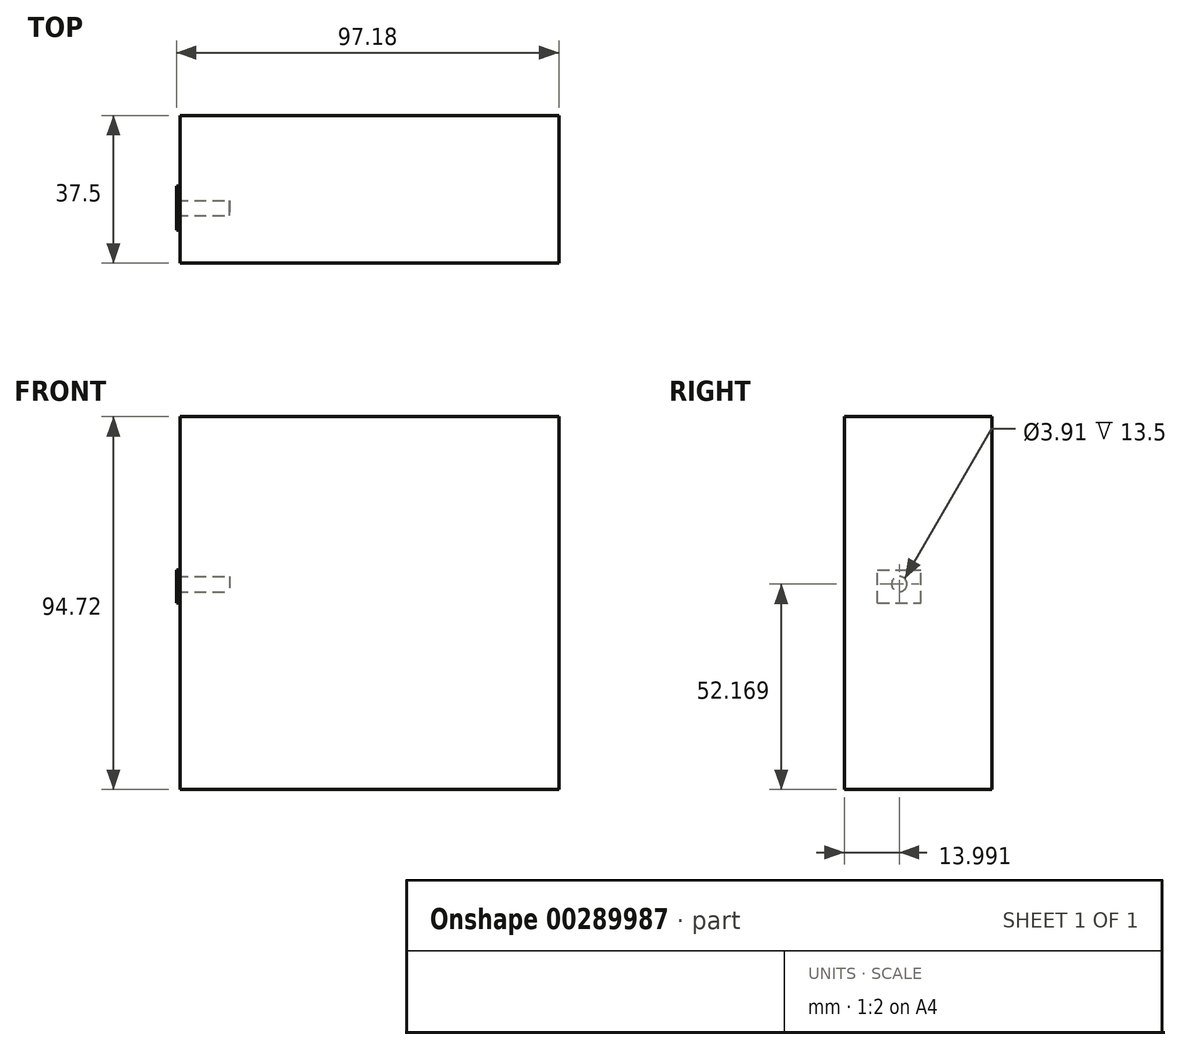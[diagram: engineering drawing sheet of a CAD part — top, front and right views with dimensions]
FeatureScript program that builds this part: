
annotation { "Feature Type Name" : "Feature", "Feature Type Description" : "" }
export const myFeature = defineFeature(function(context is Context, id is Id, definition is map)
    precondition{}
    {
        {
            var Q0;
            Q0=qCreatedBy(makeId("Front.planeOp"),FACE);
            var sketch = newSketch(context, id + "F0", { "sketchPlane" : qUnion([Q0])});
            skLineSegment(sketch, "E0.bottom", {"start": v(48.1, -47.36) * mm, "end": v(-48.1, -47.36) * mm});
            skLineSegment(sketch, "E0.top", {"start": v(48.1, 47.36) * mm, "end": v(-48.1, 47.36) * mm});
            skLineSegment(sketch, "E0.left", {"start": v(48.1, -47.36) * mm, "end": v(48.1, 47.36) * mm});
            skLineSegment(sketch, "E0.right", {"start": v(-48.1, -47.36) * mm, "end": v(-48.1, 47.36) * mm});
            skPoint(sketch, "E0.middle", {"position": v(0, 0) * mm});
            skSolve(sketch);
        }
        {
            var Q0;
            Q0=makeQuery(id+"F0.imprint","IMPRINT",FACE,{"disambiguationData":[TD([[makeQuery(id+"F0.imprint","IMPRINT",EDGE,{"derivedFrom":sQuery(id+"F0.wireOp",EDGE,"E0.bottom")}),-1.0]])]});
            extrude(context, id + "F1", {"entities" : qUnion([Q0]), "oppositeDirection" : true, "depth" : 25 * mm});
        }
        {
            var Q0;
            Q0=makeQuery(id+"F1.opExtrude","SWEPT_FACE",FACE,{"disambiguationData":[OSD([sQuery(id+"F0.wireOp",EDGE,"E0.right")])]});
            var sketch = newSketch(context, id + "F2", { "sketchPlane" : qUnion([Q0])});
            skLineSegment(sketch, "E1.bottom", {"start": v(-8.45, 0) * mm, "end": v(-19.53, 0) * mm});
            skLineSegment(sketch, "E1.top", {"start": v(-8.45, 8.45) * mm, "end": v(-19.53, 8.45) * mm});
            skLineSegment(sketch, "E1.left", {"start": v(-8.45, 0) * mm, "end": v(-8.45, 8.45) * mm});
            skLineSegment(sketch, "E1.right", {"start": v(-19.53, 0) * mm, "end": v(-19.53, 8.45) * mm});
            skPoint(sketch, "E1.middle", {"position": v(-14, 4.23) * mm});
            skPoint(sketch, "E1.cornerSnap0", {"position": v(-25, 0) * mm});
            skSolve(sketch);
        }
        {
            var Q0;
            Q0=makeQuery(id+"F2.imprint","IMPRINT",FACE,{"disambiguationData":[TD([[makeQuery(id+"F2.imprint","IMPRINT",EDGE,{"derivedFrom":sQuery(id+"F2.wireOp",EDGE,"E1.bottom")}),-1.0]])]});
            extrude(context, id + "F3", {"entities" : qUnion([Q0]), "operationType" : NewBodyOperationType.ADD, "depth" : 1 * mm});
        }
        {
            var Q0;
            Q0=makeQuery(id+"F1.opExtrude","CAP_FACE",FACE,{"disambiguationData":[OSD([sQuery(id+"F0.wireOp",EDGE,"E0.bottom"),sQuery(id+"F0.wireOp",EDGE,"E0.top"),sQuery(id+"F0.wireOp",EDGE,"E0.left"),sQuery(id+"F0.wireOp",EDGE,"E0.right")])],"isStart":false});
            var sketch = newSketch(context, id + "F4", { "sketchPlane" : qUnion([Q0])});
            skLineSegment(sketch, "E2.bottom", {"start": v(-48.1, -47.36) * mm, "end": v(48.1, -47.36) * mm});
            skLineSegment(sketch, "E2.top", {"start": v(-48.1, 47.36) * mm, "end": v(48.1, 47.36) * mm});
            skLineSegment(sketch, "E2.left", {"start": v(-48.1, -47.36) * mm, "end": v(-48.1, 47.36) * mm});
            skLineSegment(sketch, "E2.right", {"start": v(48.1, -47.36) * mm, "end": v(48.1, 47.36) * mm});
            skPoint(sketch, "E2.middle", {"position": v(0, 0) * mm});
            skSolve(sketch);
        }
        {
            var Q0;
            Q0 = qSketchRegion(id + "F4", true);
            extrude(context, id + "F5", {"entities" : qUnion([Q0]), "operationType" : NewBodyOperationType.ADD, "endBound" : BoundingType.SYMMETRIC, "depth" : 25 * mm});
        }
        {
            var Q0;
            Q0=makeQuery(id+"F5.boolean.opBoolean","MERGE",FACE,{"derivedFrom":[makeQuery(id+"F1.opExtrude","SWEPT_FACE",FACE,{"disambiguationData":[OSD([sQuery(id+"F0.wireOp",EDGE,"E0.right")])]}),makeQuery(id+"F5.opExtrude","SWEPT_FACE",FACE,{"disambiguationData":[OSD([sQuery(id+"F4.wireOp",EDGE,"E2.right")])]})]});
            var sketch = newSketch(context, id + "F6", { "sketchPlane" : qUnion([Q0])});
            skCircle(sketch, "E3", {"center": v(-14, 4.8) * mm, "radius": 1.96 * mm});
            skPoint(sketch, "E3.centerSnap0", {"position": v(-14, 0) * mm});
            skSolve(sketch);
        }
        {
            var Q0;
            Q0 = qSketchRegion(id + "F6", true);
            extrude(context, id + "F7", {"entities" : qUnion([Q0]), "operationType" : NewBodyOperationType.REMOVE, "endBound" : BoundingType.SYMMETRIC, "depth" : 25 * mm});
        }
    });
